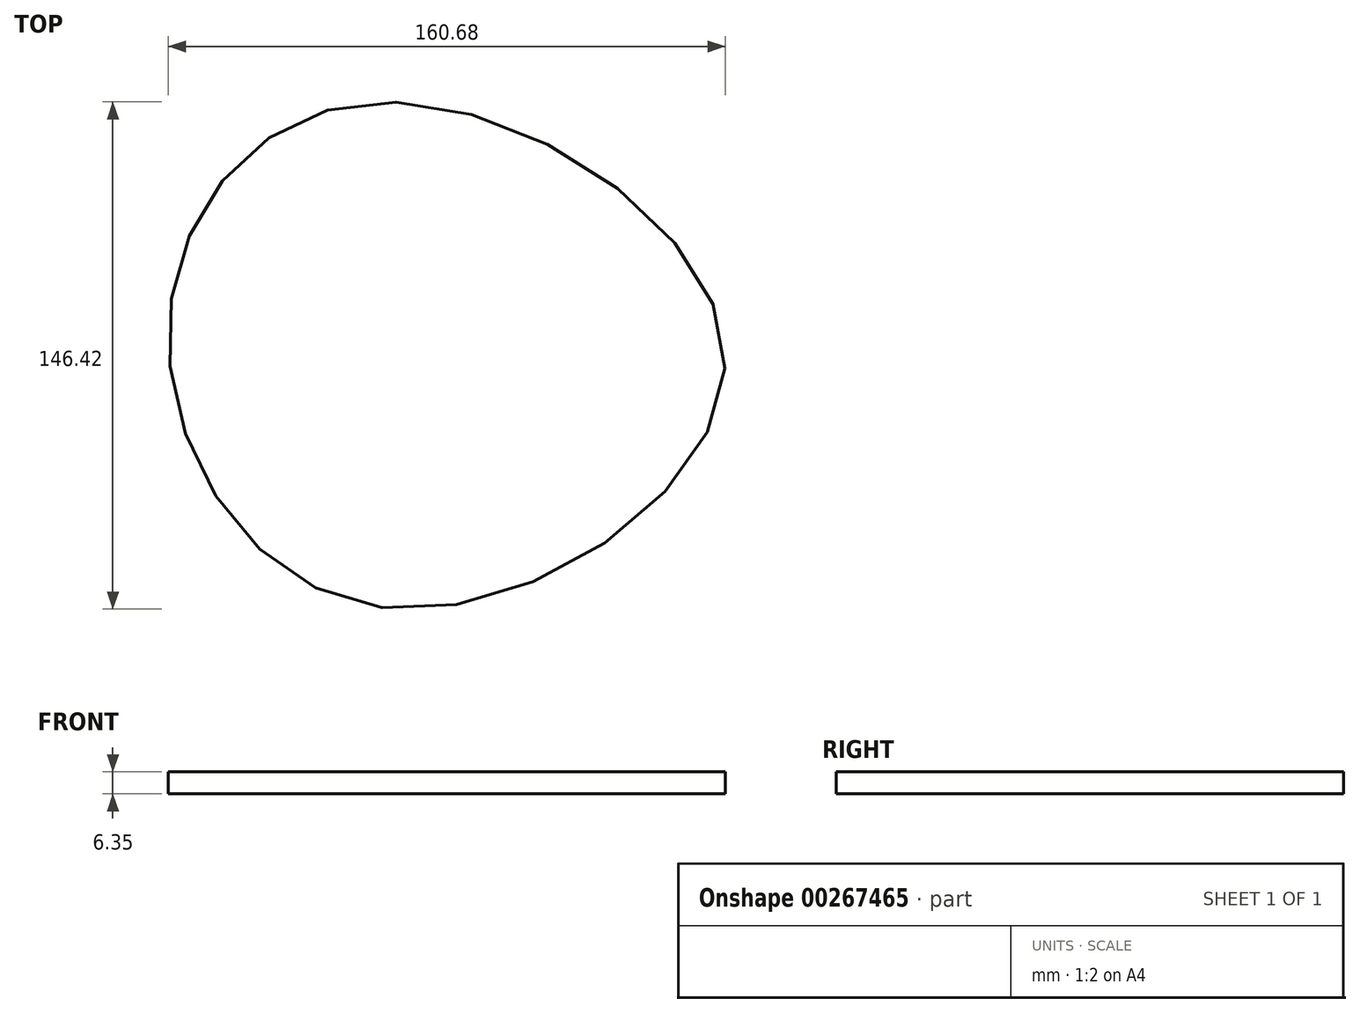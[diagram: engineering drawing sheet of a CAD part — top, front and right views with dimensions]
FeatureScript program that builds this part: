
annotation { "Feature Type Name" : "Feature", "Feature Type Description" : "" }
export const myFeature = defineFeature(function(context is Context, id is Id, definition is map)
    precondition{}
    {
        {
            var Q0;
            Q0=qCreatedBy(makeId("Top.planeOp"),FACE);
            var sketch = newSketch(context, id + "F0", { "sketchPlane" : qUnion([Q0])});
            skFitSpline(sketch, "E0", {"points": [v(0, -70.52) * mm, v(99, 0) * mm, v(-1.1, 75.4) * mm, v(-61.64, 9.98) * mm, v(0, -70.52) * mm]});
            skSolve(sketch);
        }
        {
            var Q0;
            Q0 = qSketchRegion(id + "F0", true);
            extrude(context, id + "F1", {"entities" : qUnion([Q0]), "depth" : 6.35 * mm});
        }
    });
